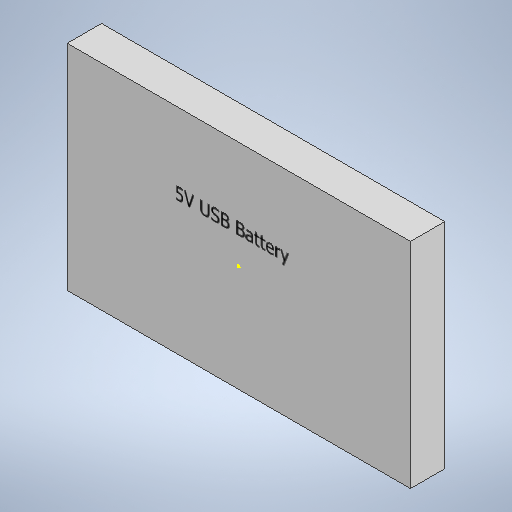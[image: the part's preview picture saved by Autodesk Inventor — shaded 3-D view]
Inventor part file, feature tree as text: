
AUTODESK INVENTOR PART (.ipt)
format: ipt  version: 2025.3 (Build 293356000, 356)  size: 191,488 bytes
history: native  units: mm
features: sketch x2, other x1, extrude x1
ambient origin geometry x8: Origin, YZ Plane, XZ Plane, XY Plane, X Axis, Y Axis, Z Axis, Center Point
bodies: Body1 (feature_tree)
feature tree (4):
  other  "ソリッド1"
  extrude  "押し出し1"  Depth=85.0mm
  sketch  "スケッチ2"
  sketch  "スケッチ1"
